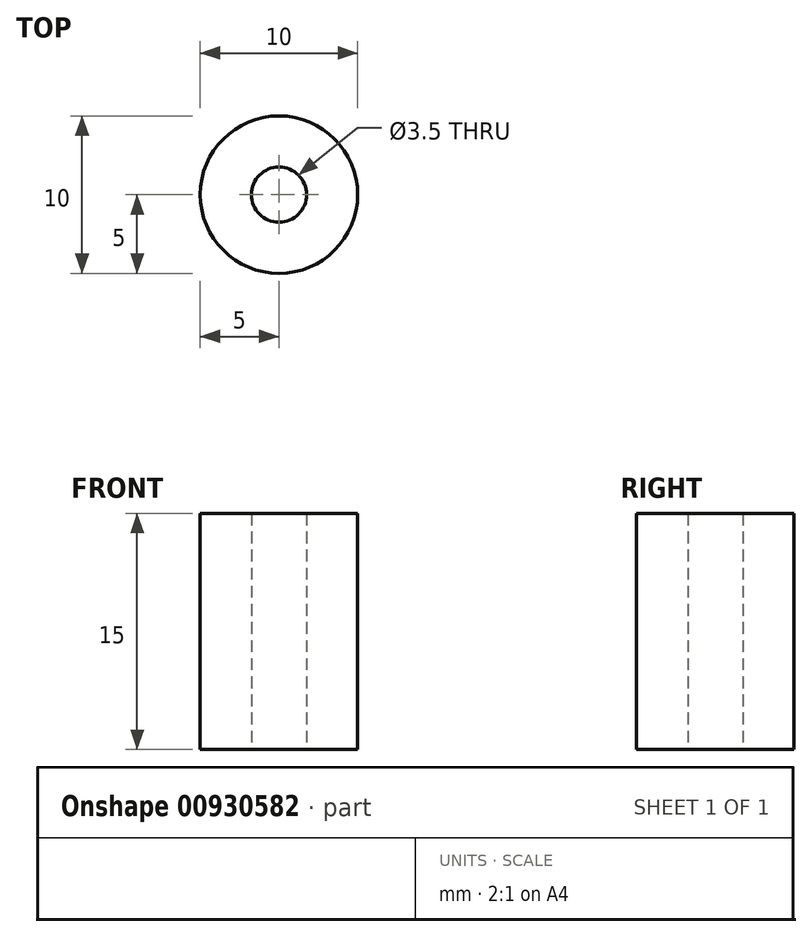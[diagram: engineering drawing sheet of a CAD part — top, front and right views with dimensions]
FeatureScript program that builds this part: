
annotation { "Feature Type Name" : "Feature", "Feature Type Description" : "" }
export const myFeature = defineFeature(function(context is Context, id is Id, definition is map)
    precondition{}
    {
        {
            var Q0;
            Q0=qCreatedBy(makeId("Top.planeOp"),FACE);
            var sketch = newSketch(context, id + "F0", { "sketchPlane" : qUnion([Q0])});
            skCircle(sketch, "E0", {"center": v(0, 0) * mm, "radius": 5 * mm});
            skCircle(sketch, "E1", {"center": v(0, 0) * mm, "radius": 1.75 * mm});
            skSolve(sketch);
        }
        {
            var Q0;
            Q0=qSketchRegion(id+"F0",true);
            extrude(context, id + "F1", {"entities" : qUnion([Q0]), "depth" : 15 * mm, "offsetDistance" : 25 * mm});
        }
    });
